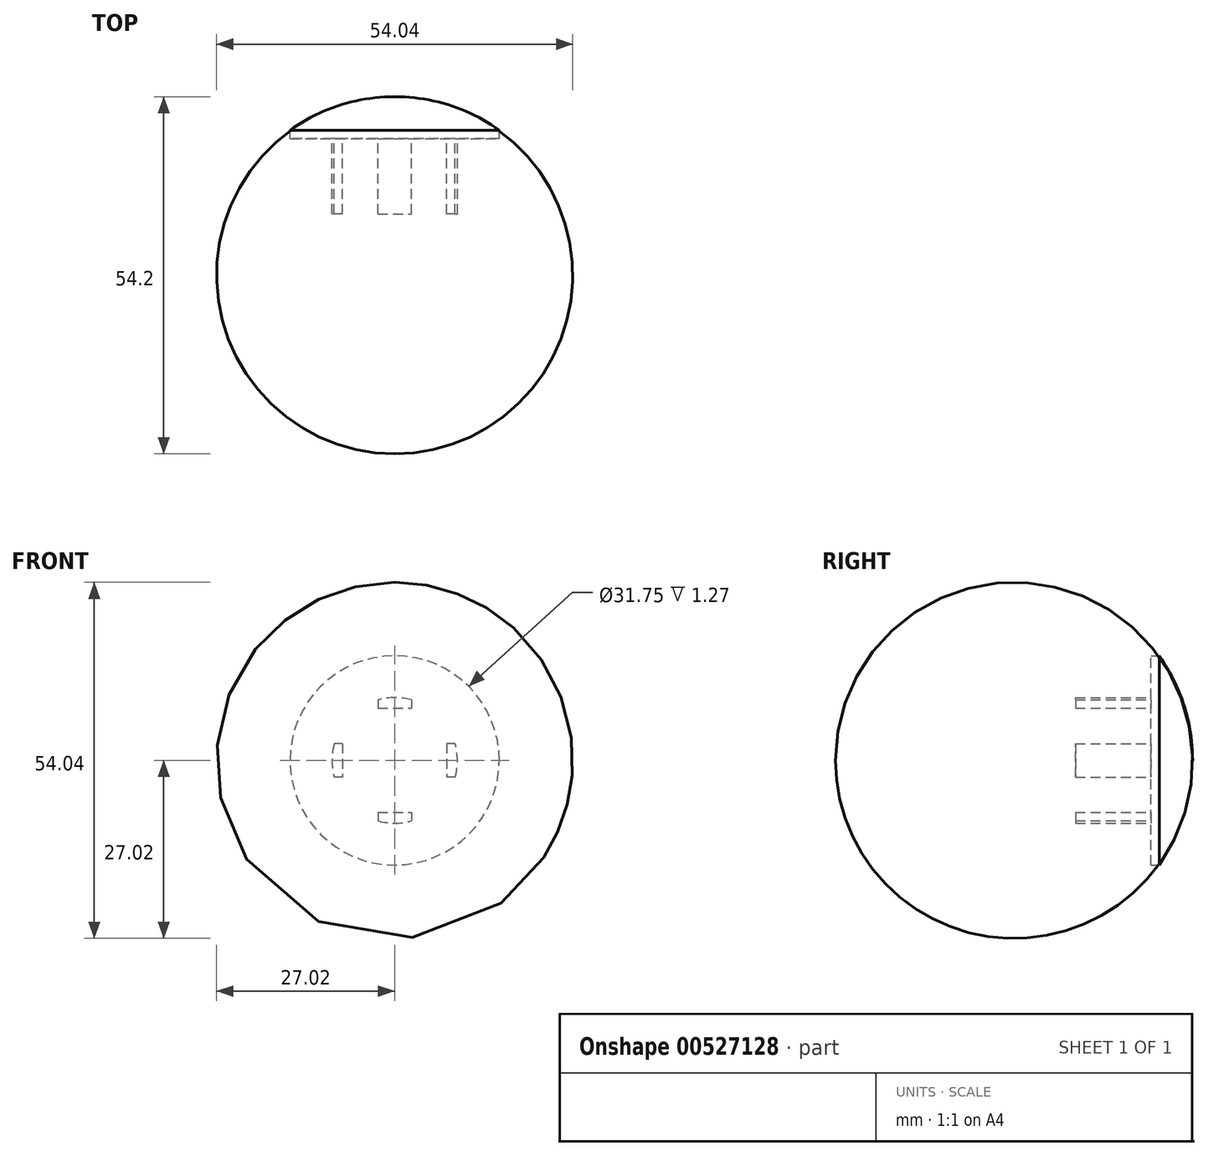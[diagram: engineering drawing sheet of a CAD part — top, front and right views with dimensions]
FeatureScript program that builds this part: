
annotation { "Feature Type Name" : "Feature", "Feature Type Description" : "" }
export const myFeature = defineFeature(function(context is Context, id is Id, definition is map)
    precondition{}
    {
        {
            var Q0;
            Q0=qCreatedBy(makeId("Front.planeOp"),FACE);
            var sketch = newSketch(context, id + "F0", { "sketchPlane" : qUnion([Q0])});
            skCircle(sketch, "E0", {"center": v(0, 0) * mm, "radius": 9.53 * mm});
            skLineSegment(sketch, "E1.bottom", {"start": v(-2.54, 9.18) * mm, "end": v(2.54, 9.18) * mm});
            skLineSegment(sketch, "E1.top", {"start": v(-2.54, -9.18) * mm, "end": v(2.54, -9.18) * mm});
            skLineSegment(sketch, "E1.left", {"start": v(-2.54, 9.18) * mm, "end": v(-2.54, -9.18) * mm});
            skLineSegment(sketch, "E1.right", {"start": v(2.54, 9.18) * mm, "end": v(2.54, -9.18) * mm});
            skLineSegment(sketch, "E2.bottom", {"start": v(9.18, 2.54) * mm, "end": v(-9.18, 2.54) * mm});
            skLineSegment(sketch, "E2.top", {"start": v(9.18, -2.54) * mm, "end": v(-9.18, -2.54) * mm});
            skLineSegment(sketch, "E2.left", {"start": v(9.18, 2.54) * mm, "end": v(9.18, -2.54) * mm});
            skLineSegment(sketch, "E2.right", {"start": v(-9.18, 2.54) * mm, "end": v(-9.18, -2.54) * mm});
            skLineSegment(sketch, "E3", {"start": v(-2.54, 7.91) * mm, "end": v(2.54, 7.91) * mm});
            skLineSegment(sketch, "E4", {"start": v(-7.91, 2.54) * mm, "end": v(-7.91, -2.54) * mm});
            skLineSegment(sketch, "E5", {"start": v(-2.54, -7.91) * mm, "end": v(2.54, -7.91) * mm});
            skLineSegment(sketch, "E6", {"start": v(7.91, 2.54) * mm, "end": v(7.91, -2.54) * mm});
            skSolve(sketch);
        }
        {
            var Q0;
            {var subQ0=sQuery(id+"F0.wireOp",EDGE,"E1.bottom");Q0=makeQuery(id+"F0.imprint","IMPRINT",FACE,{"disambiguationData":[TD([[makeQuery(id+"F0.imprint","IMPRINT",EDGE,{"derivedFrom":subQ0}),-1.0]])]});}
            var Q1;
            {var subQ0=sQuery(id+"F0.wireOp",EDGE,"E1.bottom");Q1=makeQuery(id+"F0.imprint","IMPRINT",FACE,{"disambiguationData":[TD([[makeQuery(id+"F0.imprint","IMPRINT",EDGE,{"derivedFrom":subQ0}),1.0]])]});}
            var Q2;
            {var subQ0=sQuery(id+"F0.wireOp",EDGE,"E2.right");Q2=makeQuery(id+"F0.imprint","IMPRINT",FACE,{"disambiguationData":[TD([[makeQuery(id+"F0.imprint","IMPRINT",EDGE,{"derivedFrom":subQ0}),1.0]])]});}
            var Q3;
            {var subQ0=sQuery(id+"F0.wireOp",EDGE,"E2.right");Q3=makeQuery(id+"F0.imprint","IMPRINT",FACE,{"disambiguationData":[TD([[makeQuery(id+"F0.imprint","IMPRINT",EDGE,{"derivedFrom":subQ0}),-1.0]])]});}
            var Q4;
            {var subQ0=sQuery(id+"F0.wireOp",EDGE,"E1.top");Q4=makeQuery(id+"F0.imprint","IMPRINT",FACE,{"disambiguationData":[TD([[makeQuery(id+"F0.imprint","IMPRINT",EDGE,{"derivedFrom":subQ0}),-1.0]])]});}
            var Q5;
            {var subQ0=sQuery(id+"F0.wireOp",EDGE,"E1.top");Q5=makeQuery(id+"F0.imprint","IMPRINT",FACE,{"disambiguationData":[TD([[makeQuery(id+"F0.imprint","IMPRINT",EDGE,{"derivedFrom":subQ0}),1.0]])]});}
            var Q6;
            {var subQ0=sQuery(id+"F0.wireOp",EDGE,"E2.left");Q6=makeQuery(id+"F0.imprint","IMPRINT",FACE,{"disambiguationData":[TD([[makeQuery(id+"F0.imprint","IMPRINT",EDGE,{"derivedFrom":subQ0}),-1.0]])]});}
            var Q7;
            {var subQ0=sQuery(id+"F0.wireOp",EDGE,"E2.left");Q7=makeQuery(id+"F0.imprint","IMPRINT",FACE,{"disambiguationData":[TD([[makeQuery(id+"F0.imprint","IMPRINT",EDGE,{"derivedFrom":subQ0}),1.0]])]});}
            extrude(context, id + "F1", {"entities" : qUnion([Q0, Q1, Q2, Q3, Q4, Q5, Q6, Q7]), "depth" : 12.7 * mm, "offsetDistance" : 25.4 * mm});
        }
        {
            var Q0;
            Q0=qCreatedBy(makeId("Right.planeOp"),FACE);
            var sketch = newSketch(context, id + "F2", { "sketchPlane" : qUnion([Q0])});
            skLineSegment(sketch, "E7", {"start": v(0, 0) * mm, "end": v(5.08, 0) * mm});
            skLineSegment(sketch, "E8", {"start": v(0, 15.88) * mm, "end": v(0, -15.88) * mm});
            skArc(sketch, "E9", {"start": v(5.08, 0) * mm, "mid": v(3.8, 8.34) * mm, "end": v(0, 15.88) * mm});
            skSolve(sketch);
        }
        {
            var Q0;
            {var subQ0=sQuery(id+"F2.wireOp",EDGE,"E7");Q0=makeQuery(id+"F2.imprint","IMPRINT",FACE,{"disambiguationData":[TD([[makeQuery(id+"F2.imprint","IMPRINT",EDGE,{"derivedFrom":subQ0}),1.0]])]});}
            var Q1;
            Q1=sQuery(id+"F2.wireOp",EDGE,"E7");
            revolve(context, id + "F3", {"operationType" : NewBodyOperationType.ADD, "entities" : qUnion([Q0]), "axis" : qUnion([Q1]), "revolveType" : RevolveType.FULL});
        }
        {
            var Q0;
            Q0=makeQuery(id+"F3.opRevolve","SWEPT_FACE",FACE,{"disambiguationData":[OSD([sQuery(id+"F2.wireOp",EDGE,"E8")])]});
            extrude(context, id + "F4", {"entities" : qUnion([Q0]), "operationType" : NewBodyOperationType.ADD, "depth" : 1.27 * mm, "offsetDistance" : 25.4 * mm});
        }
    });
